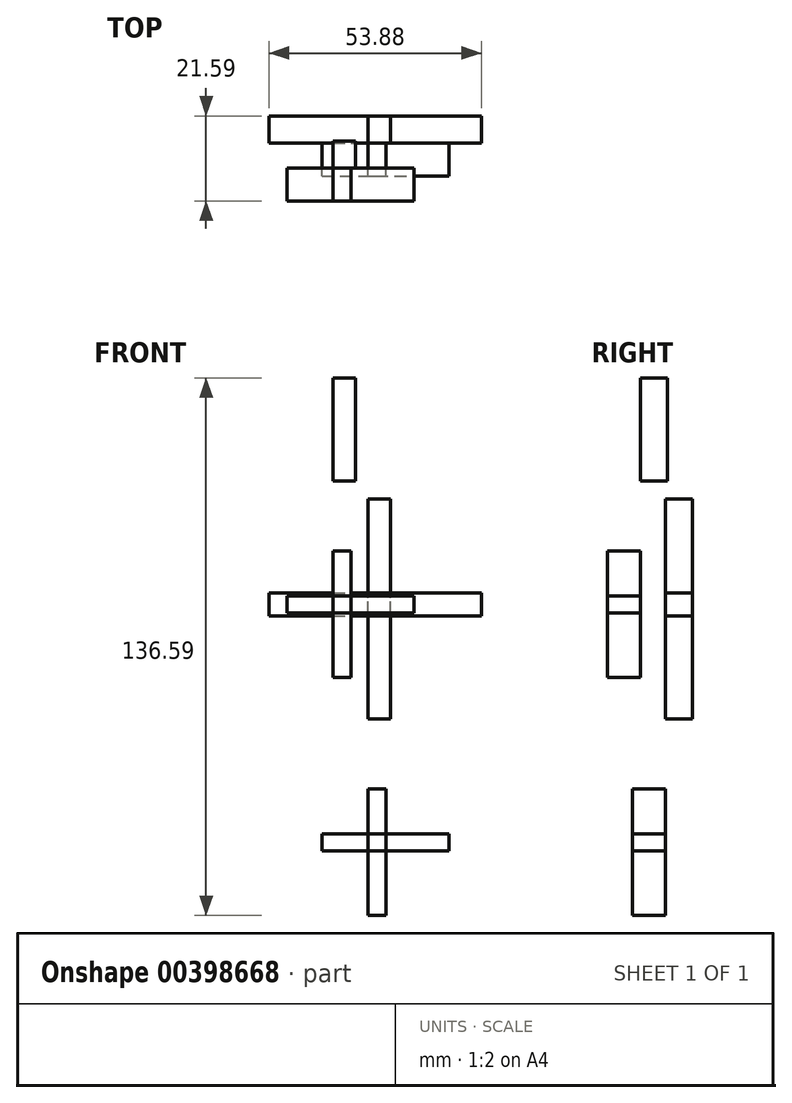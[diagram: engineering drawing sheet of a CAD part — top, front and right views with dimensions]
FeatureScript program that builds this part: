
annotation { "Feature Type Name" : "Feature", "Feature Type Description" : "" }
export const myFeature = defineFeature(function(context is Context, id is Id, definition is map)
    precondition{}
    {
        {
            var Q0;
            Q0=qCreatedBy(makeId("Front.planeOp"),FACE);
            var sketch = newSketch(context, id + "F0", { "sketchPlane" : qUnion([Q0])});
            skLineSegment(sketch, "E0.bottom", {"start": v(0, 0) * mm, "end": v(5.63, 0) * mm});
            skLineSegment(sketch, "E0.top", {"start": v(0, 55.89) * mm, "end": v(5.63, 55.89) * mm});
            skLineSegment(sketch, "E0.left", {"start": v(0, 0) * mm, "end": v(0, 55.89) * mm});
            skLineSegment(sketch, "E0.right", {"start": v(5.63, 0) * mm, "end": v(5.63, 55.89) * mm});
            skLineSegment(sketch, "E1.bottom", {"start": v(-25.13, 31.96) * mm, "end": v(28.75, 31.96) * mm});
            skLineSegment(sketch, "E1.top", {"start": v(-25.13, 26.13) * mm, "end": v(28.75, 26.13) * mm});
            skLineSegment(sketch, "E1.left", {"start": v(-25.13, 31.96) * mm, "end": v(-25.13, 26.13) * mm});
            skLineSegment(sketch, "E1.right", {"start": v(28.75, 31.96) * mm, "end": v(28.75, 26.13) * mm});
            skSolve(sketch);
        }
        {
            var Q0;
            Q0=qCreatedBy(makeId("Front.planeOp"),FACE);
            var sketch = newSketch(context, id + "F1", { "sketchPlane" : qUnion([Q0])});
            skLineSegment(sketch, "E2.bottom", {"start": v(0, -17.83) * mm, "end": v(4.5, -17.83) * mm});
            skLineSegment(sketch, "E2.top", {"start": v(0, -50) * mm, "end": v(4.5, -50) * mm});
            skLineSegment(sketch, "E2.left", {"start": v(0, -17.83) * mm, "end": v(0, -50) * mm});
            skLineSegment(sketch, "E2.right", {"start": v(4.5, -17.83) * mm, "end": v(4.5, -50) * mm});
            skSolve(sketch);
        }
        {
            var Q0;
            Q0=qCreatedBy(makeId("Front.planeOp"),FACE);
            var sketch = newSketch(context, id + "F2", { "sketchPlane" : qUnion([Q0])});
            skLineSegment(sketch, "E3.bottom", {"start": v(-11.7, -29.22) * mm, "end": v(20.48, -29.22) * mm});
            skLineSegment(sketch, "E3.top", {"start": v(-11.7, -33.62) * mm, "end": v(20.48, -33.62) * mm});
            skLineSegment(sketch, "E3.left", {"start": v(-11.7, -29.22) * mm, "end": v(-11.7, -33.62) * mm});
            skLineSegment(sketch, "E3.right", {"start": v(20.48, -29.22) * mm, "end": v(20.48, -33.62) * mm});
            skSolve(sketch);
        }
        {
            var Q0;
            {var subQ0=sQuery(id+"F0.wireOp",EDGE,"E0.top");Q0=makeQuery(id+"F0.imprint","IMPRINT",FACE,{"disambiguationData":[TD([[makeQuery(id+"F0.imprint","IMPRINT",EDGE,{"derivedFrom":subQ0}),-1.0]])]});}
            var Q1;
            {var subQ0=sQuery(id+"F0.wireOp",EDGE,"E0.bottom");Q1=makeQuery(id+"F0.imprint","IMPRINT",FACE,{"disambiguationData":[TD([[makeQuery(id+"F0.imprint","IMPRINT",EDGE,{"derivedFrom":subQ0}),1.0]])]});}
            var Q2;
            {var subQ5=sQuery(id+"F0.wireOp",EDGE,"E1.right");Q2=makeQuery(id+"F0.imprint","IMPRINT",FACE,{"disambiguationData":[TD([[makeQuery(id+"F0.imprint","IMPRINT",EDGE,{"derivedFrom":subQ5}),-1.0]])]});}
            var Q3;
            {var subQ5=sQuery(id+"F0.wireOp",EDGE,"E1.left");Q3=makeQuery(id+"F0.imprint","IMPRINT",FACE,{"disambiguationData":[TD([[makeQuery(id+"F0.imprint","IMPRINT",EDGE,{"derivedFrom":subQ5}),1.0]])]});}
            extrude(context, id + "F3", {"entities" : qUnion([Q0, Q1, Q2, Q3]), "oppositeDirection" : true, "depth" : 6.86 * mm});
        }
        {
            var Q0;
            Q0=makeQuery(id+"F1.imprint","IMPRINT",FACE,{"disambiguationData":[TD([[makeQuery(id+"F1.imprint","IMPRINT",EDGE,{"derivedFrom":sQuery(id+"F1.wireOp",EDGE,"E2.bottom")}),-1.0]])]});
            var Q1;
            Q1=makeQuery(id+"F2.imprint","IMPRINT",FACE,{"disambiguationData":[TD([[makeQuery(id+"F2.imprint","IMPRINT",EDGE,{"derivedFrom":sQuery(id+"F2.wireOp",EDGE,"E3.bottom")}),-1.0]])]});
            extrude(context, id + "F4", {"entities" : qUnion([Q0, Q1]), "operationType" : NewBodyOperationType.ADD, "depth" : 8.38 * mm});
        }
        {
            var Q0;
            Q0=makeQuery(id+"F4.opExtrude","SWEPT_BODY",BODY,{"disambiguationData":[OSD([sQuery(id+"F2.wireOp",EDGE,"E3.bottom"),sQuery(id+"F2.wireOp",EDGE,"E3.top"),sQuery(id+"F2.wireOp",EDGE,"E3.left"),sQuery(id+"F2.wireOp",EDGE,"E3.right")])]});
            var Q1;
            Q1=makeQuery(id+"F4.opExtrude","SWEPT_BODY",BODY,{"disambiguationData":[OSD([sQuery(id+"F1.wireOp",EDGE,"E2.bottom"),sQuery(id+"F1.wireOp",EDGE,"E2.top"),sQuery(id+"F1.wireOp",EDGE,"E2.left"),sQuery(id+"F1.wireOp",EDGE,"E2.right")])]});
            var Q2;
            Q2=makeQuery(id+"F3.opExtrude","SWEPT_BODY",BODY,{"disambiguationData":[OSD([sQuery(id+"F0.wireOp",EDGE,"E0.bottom"),sQuery(id+"F0.wireOp",EDGE,"E0.left"),sQuery(id+"F0.wireOp",EDGE,"E0.right"),sQuery(id+"F0.wireOp",EDGE,"E1.top")])]});
            transform(context, id + "F5", {"entities" : qUnion([Q0, Q1, Q2]), "transformType" : TransformType.TRANSLATION_3D, "dx" : -8.9 * mm, "dy" : -6.35 * mm, "dz" : 60.45 * mm, "makeCopy" : true});
        }
    });
